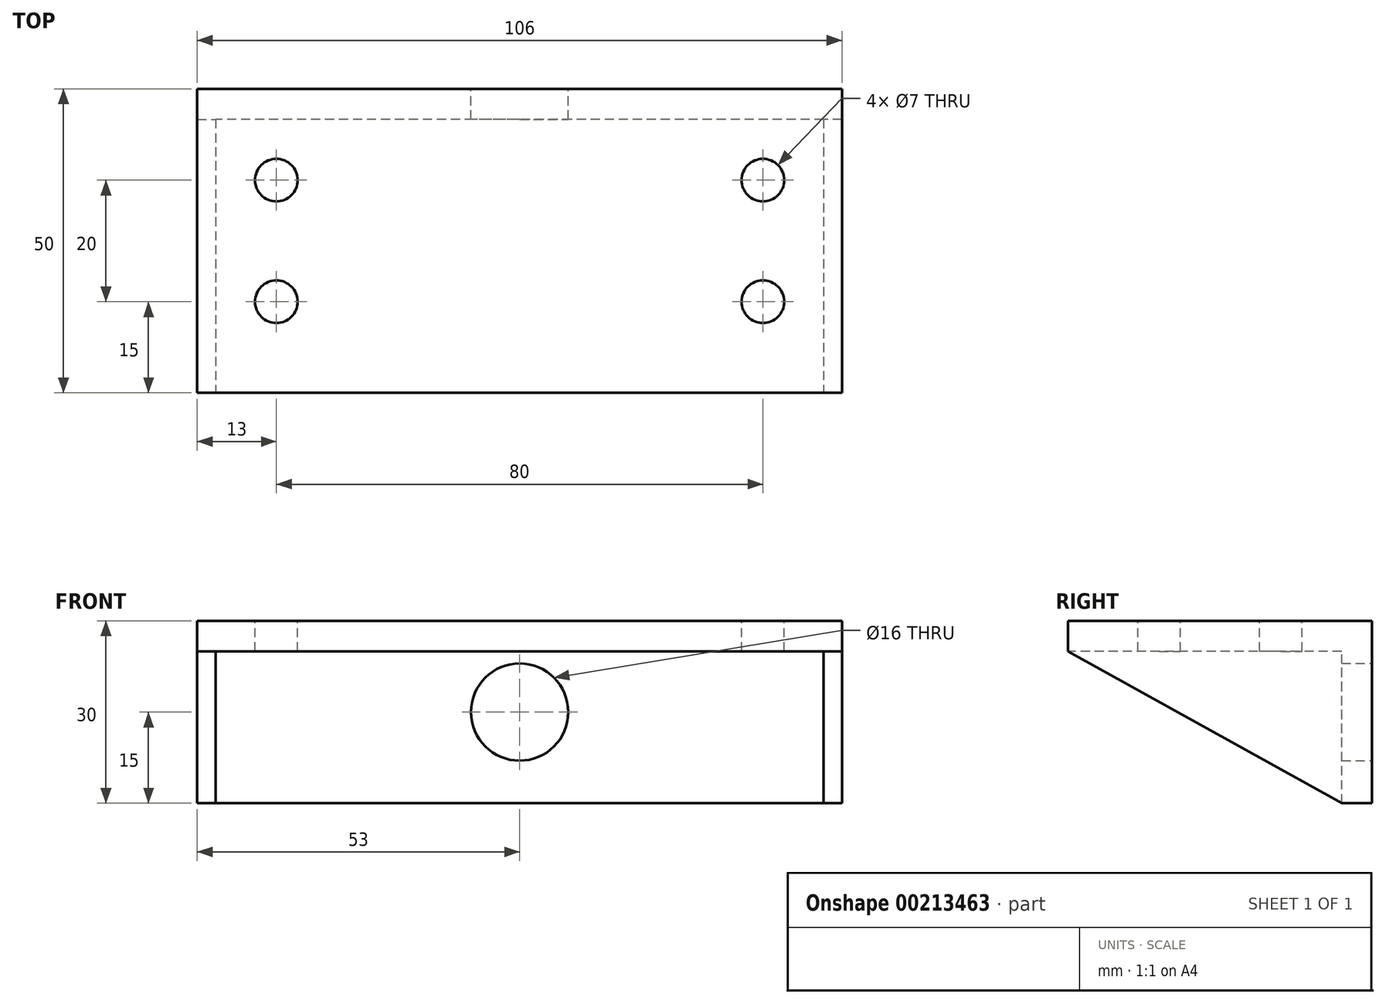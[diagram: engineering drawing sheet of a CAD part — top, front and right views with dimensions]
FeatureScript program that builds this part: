
annotation { "Feature Type Name" : "Feature", "Feature Type Description" : "" }
export const myFeature = defineFeature(function(context is Context, id is Id, definition is map)
    precondition{}
    {
        {
            var Q0;
            Q0=qCreatedBy(makeId("Right.planeOp"),FACE);
            var sketch = newSketch(context, id + "F0", { "sketchPlane" : qUnion([Q0])});
            skLineSegment(sketch, "E0", {"start": v(-50, 0) * mm, "end": v(0, 0) * mm});
            skLineSegment(sketch, "E1", {"start": v(0, 0) * mm, "end": v(0, -30) * mm});
            skLineSegment(sketch, "E2", {"start": v(0, -30) * mm, "end": v(-5, -30) * mm});
            skLineSegment(sketch, "E3", {"start": v(-5, -30) * mm, "end": v(-5, -5) * mm});
            skLineSegment(sketch, "E4", {"start": v(-5, -5) * mm, "end": v(-50, -5) * mm});
            skLineSegment(sketch, "E5", {"start": v(-50, -5) * mm, "end": v(-50, 0) * mm});
            skSolve(sketch);
        }
        {
            var Q0;
            Q0=makeQuery(id+"F0.imprint","IMPRINT",FACE,{"disambiguationData":[TD([[makeQuery(id+"F0.imprint","IMPRINT",EDGE,{"derivedFrom":sQuery(id+"F0.wireOp",EDGE,"E0")}),-1.0]])]});
            extrude(context, id + "F1", {"entities" : qUnion([Q0]), "depth" : 100 * mm});
        }
        {
            var Q0;
            Q0=makeQuery(id+"F1.opExtrude","SWEPT_FACE",FACE,{"disambiguationData":[OSD([sQuery(id+"F0.wireOp",EDGE,"E0")])]});
            var sketch = newSketch(context, id + "F2", { "sketchPlane" : qUnion([Q0])});
            skLineSegment(sketch, "E6", {"start": v(50, -50) * mm, "end": v(50, 0) * mm, "construction": true});
            skLineSegment(sketch, "E7", {"start": v(0, -25) * mm, "end": v(100, -25) * mm, "construction": true});
            skCircle(sketch, "E8", {"center": v(10, -35) * mm, "radius": 3.5 * mm});
            skCircle(sketch, "E9.MirrorC", {"center": v(10, -15) * mm, "radius": 3.5 * mm});
            skCircle(sketch, "E10.MirrorC", {"center": v(90, -35) * mm, "radius": 3.5 * mm});
            skCircle(sketch, "E11.MirrorC", {"center": v(90, -15) * mm, "radius": 3.5 * mm});
            skSolve(sketch);
        }
        {
            var Q0;
            Q0 = qSketchRegion(id + "F2", true);
            extrude(context, id + "F3", {"entities" : qUnion([Q0]), "operationType" : NewBodyOperationType.REMOVE, "endBound" : BoundingType.THROUGH_ALL, "oppositeDirection" : true, "depth" : 25 * mm});
        }
        {
            var Q0;
            Q0=makeQuery(id+"F1.opExtrude","SWEPT_FACE",FACE,{"disambiguationData":[OSD([sQuery(id+"F0.wireOp",EDGE,"E1")])]});
            var sketch = newSketch(context, id + "F4", { "sketchPlane" : qUnion([Q0])});
            skCircle(sketch, "E12", {"center": v(-50, -15) * mm, "radius": 8 * mm});
            skSolve(sketch);
        }
        {
            var Q0;
            Q0=makeQuery(id+"F4.imprint","IMPRINT",FACE,{"disambiguationData":[TD([[makeQuery(id+"F4.imprint","IMPRINT",EDGE,{"derivedFrom":sQuery(id+"F4.wireOp",EDGE,"E12")}),1.0]])]});
            extrude(context, id + "F5", {"entities" : qUnion([Q0]), "operationType" : NewBodyOperationType.REMOVE, "endBound" : BoundingType.THROUGH_ALL, "oppositeDirection" : true, "depth" : 25 * mm});
        }
        {
            var Q0;
            Q0=makeQuery(id+"F1.opExtrude","CAP_FACE",FACE,{"disambiguationData":[OSD([sQuery(id+"F0.wireOp",EDGE,"E0"),sQuery(id+"F0.wireOp",EDGE,"E1"),sQuery(id+"F0.wireOp",EDGE,"E2"),sQuery(id+"F0.wireOp",EDGE,"E3"),sQuery(id+"F0.wireOp",EDGE,"E4"),sQuery(id+"F0.wireOp",EDGE,"E5")])],"isStart":false});
            var sketch = newSketch(context, id + "F6", { "sketchPlane" : qUnion([Q0])});
            skLineSegment(sketch, "E13", {"start": v(-50, 0) * mm, "end": v(0, 0) * mm});
            skLineSegment(sketch, "E14", {"start": v(0, 0) * mm, "end": v(0, -30) * mm});
            skLineSegment(sketch, "E15", {"start": v(0, -30) * mm, "end": v(-5, -30) * mm});
            skLineSegment(sketch, "E16", {"start": v(-5, -30) * mm, "end": v(-50, -5) * mm});
            skLineSegment(sketch, "E17", {"start": v(-50, -5) * mm, "end": v(-50, 0) * mm});
            skSolve(sketch);
        }
        {
            var Q0;
            Q0 = qSketchRegion(id + "F6", true);
            extrude(context, id + "F7", {"entities" : qUnion([Q0]), "operationType" : NewBodyOperationType.ADD, "depth" : 3 * mm});
        }
        {
            var Q0;
            Q0=makeQuery(id+"F1.opExtrude","CAP_FACE",FACE,{"disambiguationData":[OSD([sQuery(id+"F0.wireOp",EDGE,"E0"),sQuery(id+"F0.wireOp",EDGE,"E1"),sQuery(id+"F0.wireOp",EDGE,"E2"),sQuery(id+"F0.wireOp",EDGE,"E3"),sQuery(id+"F0.wireOp",EDGE,"E4"),sQuery(id+"F0.wireOp",EDGE,"E5")])],"isStart":true});
            var sketch = newSketch(context, id + "F8", { "sketchPlane" : qUnion([Q0])});
            skLineSegment(sketch, "E18", {"start": v(50, 0) * mm, "end": v(50, -5) * mm});
            skLineSegment(sketch, "E19", {"start": v(50, -5) * mm, "end": v(5, -30) * mm});
            skLineSegment(sketch, "E20", {"start": v(5, -30) * mm, "end": v(0, -30) * mm});
            skLineSegment(sketch, "E21", {"start": v(0, -30) * mm, "end": v(0, 0) * mm});
            skLineSegment(sketch, "E22", {"start": v(0, 0) * mm, "end": v(50, 0) * mm});
            skSolve(sketch);
        }
        {
            var Q0;
            Q0 = qSketchRegion(id + "F8", true);
            extrude(context, id + "F9", {"entities" : qUnion([Q0]), "operationType" : NewBodyOperationType.ADD, "depth" : 3 * mm});
        }
    });
